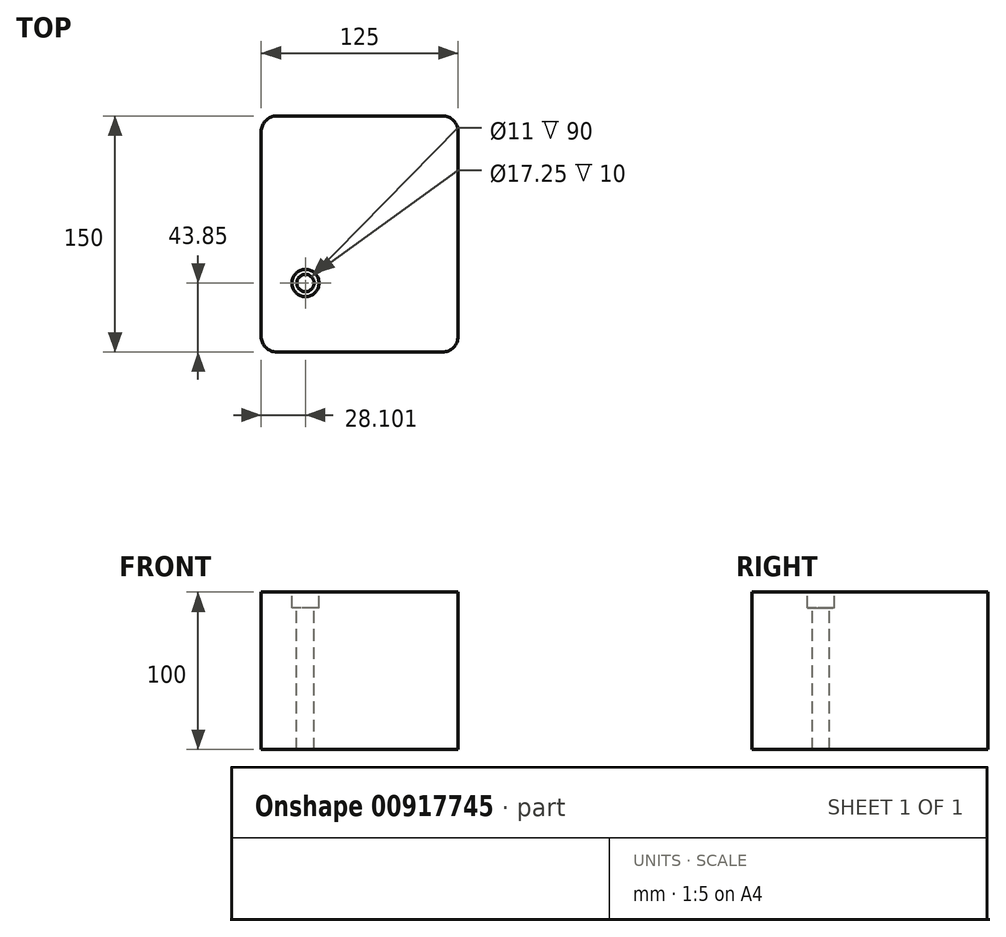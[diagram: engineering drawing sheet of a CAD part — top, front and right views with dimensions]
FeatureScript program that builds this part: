
annotation { "Feature Type Name" : "Feature", "Feature Type Description" : "" }
export const myFeature = defineFeature(function(context is Context, id is Id, definition is map)
    precondition{}
    {
        {
            var Q0;
            Q0=qCreatedBy(makeId("Front.planeOp"),FACE);
            var sketch = newSketch(context, id + "F0", { "sketchPlane" : qUnion([Q0])});
            skLineSegment(sketch, "E0.bottom", {"start": v(62.5, 50) * mm, "end": v(-62.5, 50) * mm});
            skLineSegment(sketch, "E0.top", {"start": v(62.5, -50) * mm, "end": v(-62.5, -50) * mm});
            skLineSegment(sketch, "E0.left", {"start": v(62.5, 50) * mm, "end": v(62.5, -50) * mm});
            skLineSegment(sketch, "E0.right", {"start": v(-62.5, 50) * mm, "end": v(-62.5, -50) * mm});
            skPoint(sketch, "E0.middle", {"position": v(0, 0) * mm});
            skSolve(sketch);
        }
        {
            var Q0;
            Q0=makeQuery(id+"F0.imprint","IMPRINT",FACE,{"disambiguationData":[TD([[makeQuery(id+"F0.imprint","IMPRINT",EDGE,{"derivedFrom":sQuery(id+"F0.wireOp",EDGE,"E0.bottom")}),1.0]])]});
            extrude(context, id + "F1", {"entities" : qUnion([Q0]), "depth" : 75 * mm, "offsetDistance" : 25.4 * mm, "hasSecondDirection" : true, "secondDirectionOppositeDirection" : true, "secondDirectionDepth" : 75 * mm});
        }
        {
            var Q0;
            Q0=makeQuery(id+"F1.opExtrude","CAP_EDGE",EDGE,{"disambiguationData":[OSD([sQuery(id+"F0.wireOp",EDGE,"E0.left")])],"isStart":false});
            var Q1;
            Q1=makeQuery(id+"F1.opExtrude","CAP_EDGE",EDGE,{"disambiguationData":[OSD([sQuery(id+"F0.wireOp",EDGE,"E0.left")])],"isStart":true});
            var Q2;
            Q2=makeQuery(id+"F1.opExtrude","CAP_EDGE",EDGE,{"disambiguationData":[OSD([sQuery(id+"F0.wireOp",EDGE,"E0.right")])],"isStart":true});
            var Q3;
            Q3=makeQuery(id+"F1.opExtrude","CAP_EDGE",EDGE,{"disambiguationData":[OSD([sQuery(id+"F0.wireOp",EDGE,"E0.right")])],"isStart":false});
            fillet(context, id + "F2", {"entities" : qUnion([Q0, Q1, Q2, Q3]), "radius" : 10 * mm, "tangentPropagation" : true, "allowEdgeOverflow" : false});
        }
        {
            var Q0;
            Q0=makeQuery(id+"F1.opExtrude","SWEPT_FACE",FACE,{"disambiguationData":[OSD([sQuery(id+"F0.wireOp",EDGE,"E0.bottom")])]});
            var sketch = newSketch(context, id + "F3", { "sketchPlane" : qUnion([Q0])});
            skPoint(sketch, "E1", {"position": v(-34.4, -31.15) * mm});
            skSolve(sketch);
        }
        {
            var Q0;
            Q0=sQuery(id+"F3.wireOp",VERTEX,"E1");
            var Q1;
            Q1=makeQuery(id+"F1.opExtrude","SWEPT_BODY",BODY,{"disambiguationData":[OSD([sQuery(id+"F0.wireOp",EDGE,"E0.bottom"),sQuery(id+"F0.wireOp",EDGE,"E0.top"),sQuery(id+"F0.wireOp",EDGE,"E0.left"),sQuery(id+"F0.wireOp",EDGE,"E0.right")])]});
            hole(context, id + "F4", {"style" : HoleStyle.C_BORE, "endStyle" : HoleEndStyle.THROUGH, "standardTappedOrClearance" : lookupTablePath({ "fit" : "Normal", "standard" : "ISO", "size" : "M10", "type" : "Clearance" }), "standardBlindInLast" : lookupTablePath({ "fit" : "Normal", "standard" : "ISO", "size" : "M10", "type" : "Clearance" }), "holeDiameter" : 11 * mm, "cBoreDiameter" : 17.25 * mm, "cBoreDepth" : 10 * mm, "majorDiameter" : 5 * mm, "isTappedThrough" : true, "tappedDepth" : 12 * mm, "tapClearance" : 3, "startFromSketch" : true, "locations" : qUnion([Q0]), "scope" : qUnion([Q1])});
        }
    });
